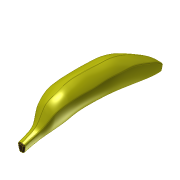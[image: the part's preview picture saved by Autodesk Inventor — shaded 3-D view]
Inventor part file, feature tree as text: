
AUTODESK INVENTOR PART (.ipt)
format: ipt  version: 2014 SP2 (Build 180246200, 246)  size: 745,984 bytes
history: native  units: mm
features: sketch x13, plane x12, fillet x3, loft x1
ambient origin geometry x8: Origin, YZ Plane, XZ Plane, XY Plane, X Axis, Y Axis, Z Axis, Center Point
bodies: Volumenkörper1 (feature_tree)
feature tree (29):
  sketch  "Skizze1"  dims[d0=20.0mm d1=20.0mm d2=20.0mm d3=20.0mm d4=20.0mm]
  plane  "Arbeitsebene1"
  sketch  "Skizze2"  dims[d5=10.0mm]
  plane  "Arbeitsebene2"
  sketch  "Skizze3"  dims[d6=-20.0mm]
  plane  "Arbeitsebene3"
  sketch  "Skizze4"  dims[d7=-15.0mm]
  plane  "Arbeitsebene4"
  sketch  "Skizze5"  dims[d8=-15.0mm]
  plane  "Arbeitsebene5"
  sketch  "Skizze6"  dims[d9=-15.0mm]
  plane  "Arbeitsebene6"
  sketch  "Skizze7"  dims[d10=-15.0mm]
  plane  "Arbeitsebene7"
  sketch  "Skizze8"  dims[d11=-6.75mm]
  plane  "Arbeitsebene8"
  sketch  "Skizze9"  dims[d12=0.0mm d13=90.0deg]
  plane  "Arbeitsebene9"
  sketch  "Skizze10"  dims[d14=0.0mm d15=90.0deg]
  plane  "Arbeitsebene10"
  sketch  "Skizze11"  dims[d16=0.0mm d17=90.0deg]
  plane  "Arbeitsebene11"
  sketch  "Skizze12"  dims[d18=0.0mm d19=90.0deg]
  plane  "Arbeitsebene12"
  loft  "Erhebung1"
  fillet  "Rundung1"  Radius=20.0mm
  fillet  "Rundung2"  Radius=20.0mm
  fillet  "Rundung4"  Radius=20.0mm
  sketch  "Skizze13"  dims[d20=0.0mm d21=90.0deg d22=0.0mm d23=90.0deg d24=0.0mm d25=90.0deg d26=0.0mm d27=90.0deg d28=0.0mm d29=90.0deg d30=0.0mm d31=90.0deg d32=0.0mm d33=90.0deg d34=0.0mm d35=90.0deg d36=0.0mm d37=90.0deg d38=2.0mm d39=2.0mm d41=2.0mm]
